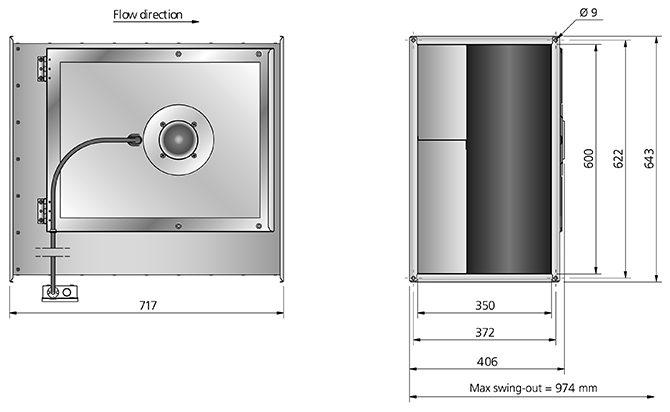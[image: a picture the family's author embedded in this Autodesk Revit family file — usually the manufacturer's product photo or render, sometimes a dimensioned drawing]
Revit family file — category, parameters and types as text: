
# Revit family: RKB 600X350 D3 ErP AC_7480161
name_source: partatom
category: Mechanical Equipment
revit_build: Autodesk Revit MEP 2014 (Build: 20130308_1515(x64)
units: mm (PartAtom-declared; Revit-internal decimal feet)

## types (1)
- RKB 600X350 D3 ErP AC
    Capacitor = - μF
    Connector Height = 350 mm  [stored 1.14829 ft]
    Connector Width = 600 mm
    Current = 1 A
    Depth = 643 mm  [stored 2.10958 ft]
    Description = UNINSULATED DUCT FANS WITH RECTANGULAR CONNECTIONS
    Frequency = 50 Hz
    Height = 406 mm  [stored 1.33202 ft]
    Main Material = Steel, Galvanized
    Max. temperature of transported air = 60 °C
    Max. temperature of transported air when speed controlled = 60 °C
    Phase = 3
    Power = 424 W
    Sound pressure level at 3 m = 55 dB(A)
    Speed = 1330 rpm
    Voltage = 400 V
    Voltage range = 380-418 V
    Weight = 30.40 kg
    Width = 717 mm  [stored 2.35236 ft]
    Wiring diagram = Y 4040004 / Δ4040003

note: [stored X ft] marks values corroborated as IEEE doubles in the binary element streams (Revit-internal decimal feet)

## geometry (parser evidence)
native form markers: Sweep x4
no freeform markers — native parametric forms only
